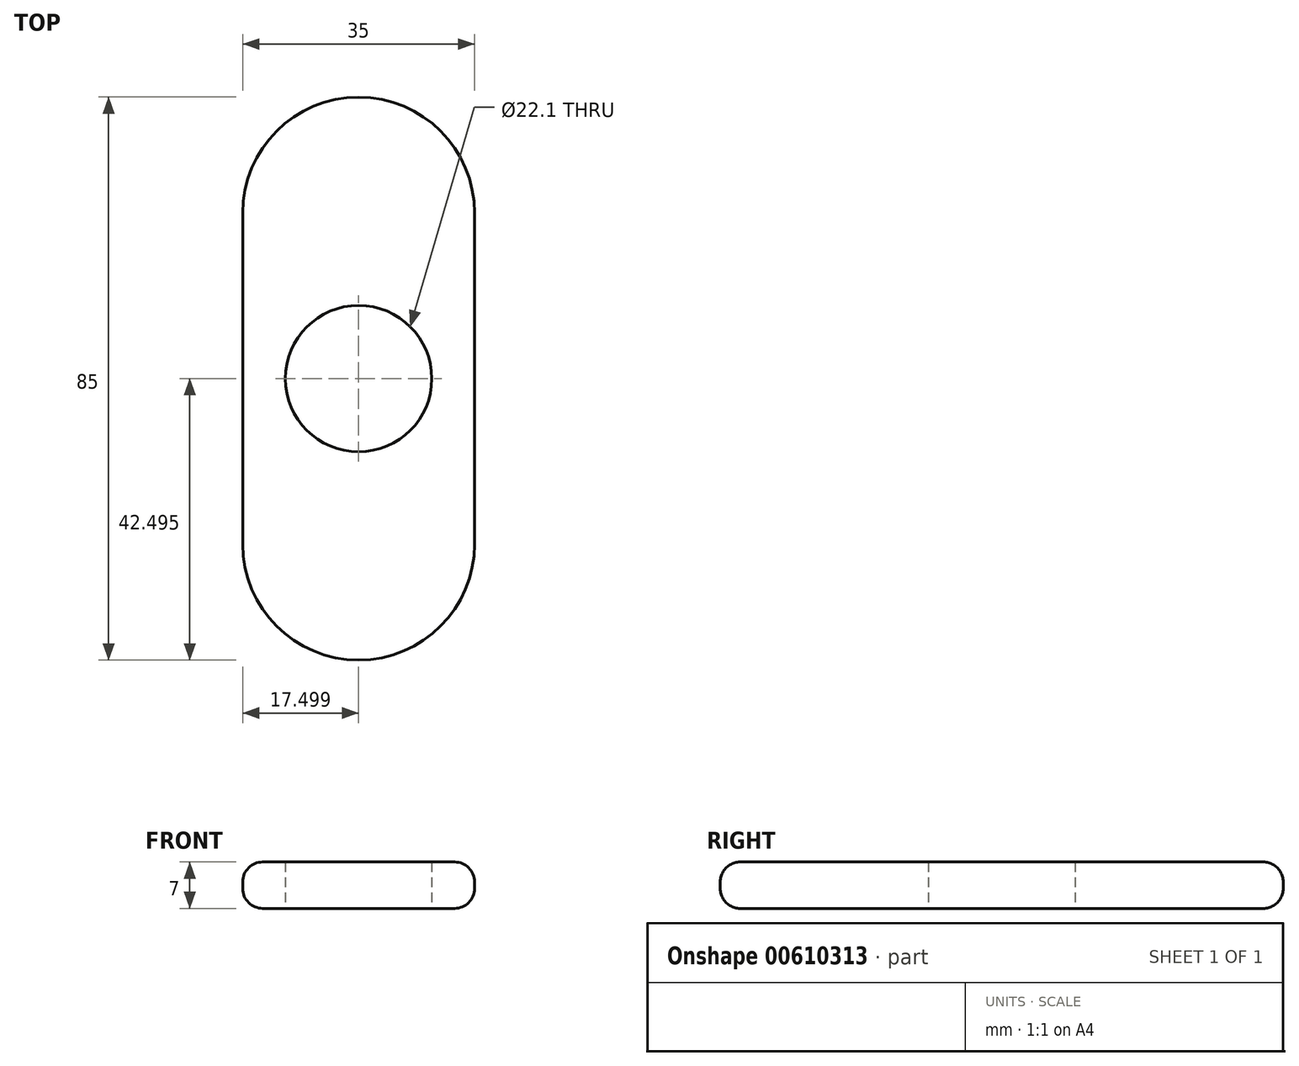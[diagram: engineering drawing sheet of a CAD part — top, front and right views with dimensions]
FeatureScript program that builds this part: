
annotation { "Feature Type Name" : "Feature", "Feature Type Description" : "" }
export const myFeature = defineFeature(function(context is Context, id is Id, definition is map)
    precondition{}
    {
        {
            var Q0;
            Q0=qCreatedBy(makeId("Top.planeOp"),FACE);
            var sketch = newSketch(context, id + "F0", { "sketchPlane" : qUnion([Q0])});
            skLineSegment(sketch, "E0", {"start": v(-17.8, 31.17) * mm, "end": v(-17.8, -18.83) * mm});
            skLineSegment(sketch, "E1", {"start": v(17.2, 31.17) * mm, "end": v(17.2, -18.83) * mm});
            skLineSegment(sketch, "E2", {"start": v(17.2, 31.17) * mm, "end": v(-17.8, 31.17) * mm});
            skLineSegment(sketch, "E3", {"start": v(17.2, -18.83) * mm, "end": v(-17.8, -18.83) * mm});
            skArc(sketch, "E4", {"start": v(17.2, 31.17) * mm, "mid": v(-0.3, 48.67) * mm, "end": v(-17.8, 31.17) * mm});
            skArc(sketch, "E5", {"start": v(-17.8, -18.83) * mm, "mid": v(-0.3, -36.33) * mm, "end": v(17.2, -18.83) * mm});
            skLineSegment(sketch, "E6", {"start": v(-17.8, 31.17) * mm, "end": v(17.2, -18.83) * mm});
            skLineSegment(sketch, "E7", {"start": v(17.2, 31.17) * mm, "end": v(-17.8, -18.83) * mm});
            skPoint(sketch, "E8", {"position": v(0, 6.58) * mm});
            skPoint(sketch, "E9", {"position": v(-0.3, 6.17) * mm});
            skSolve(sketch);
        }
        {
            var Q0;
            Q0 = qSketchRegion(id + "F0", true);
            extrude(context, id + "F1", {"entities" : qUnion([Q0]), "depth" : 7 * mm, "offsetDistance" : 25 * mm});
        }
        {
            var Q0;
            Q0=sQuery(id+"F0.wireOp",VERTEX,"E9");
            var Q1;
            Q1=makeQuery(id+"F1.opExtrude","SWEPT_BODY",BODY,{"disambiguationData":[OSD([sQuery(id+"F0.wireOp",EDGE,"E1"),sQuery(id+"F0.wireOp",EDGE,"E0"),sQuery(id+"F0.wireOp",EDGE,"E4"),sQuery(id+"F0.wireOp",EDGE,"E5")])]});
            hole(context, id + "F2", {"style" : HoleStyle.SIMPLE, "endStyle" : HoleEndStyle.THROUGH, "oppositeDirection" : true, "holeDiameter" : 22.1 * mm, "majorDiameter" : 5 * mm, "isTappedThrough" : true, "tappedDepth" : 12.7 * mm, "tapClearance" : 3, "locations" : qUnion([Q0]), "scope" : qUnion([Q1])});
        }
        {
            var Q0;
            Q0=makeQuery(id+"F1.opExtrude","SWEPT_FACE",FACE,{"disambiguationData":[OSD([sQuery(id+"F0.wireOp",EDGE,"E1")])]});
            var Q1;
            Q1=makeQuery(id+"F1.opExtrude","SWEPT_FACE",FACE,{"disambiguationData":[OSD([sQuery(id+"F0.wireOp",EDGE,"E5")])]});
            var Q2;
            Q2=makeQuery(id+"F1.opExtrude","SWEPT_FACE",FACE,{"disambiguationData":[OSD([sQuery(id+"F0.wireOp",EDGE,"E0")])]});
            fillet(context, id + "F3", {"entities" : qUnion([Q0, Q1, Q2]), "radius" : 3 * mm, "tangentPropagation" : true, "allowEdgeOverflow" : false});
        }
    });
